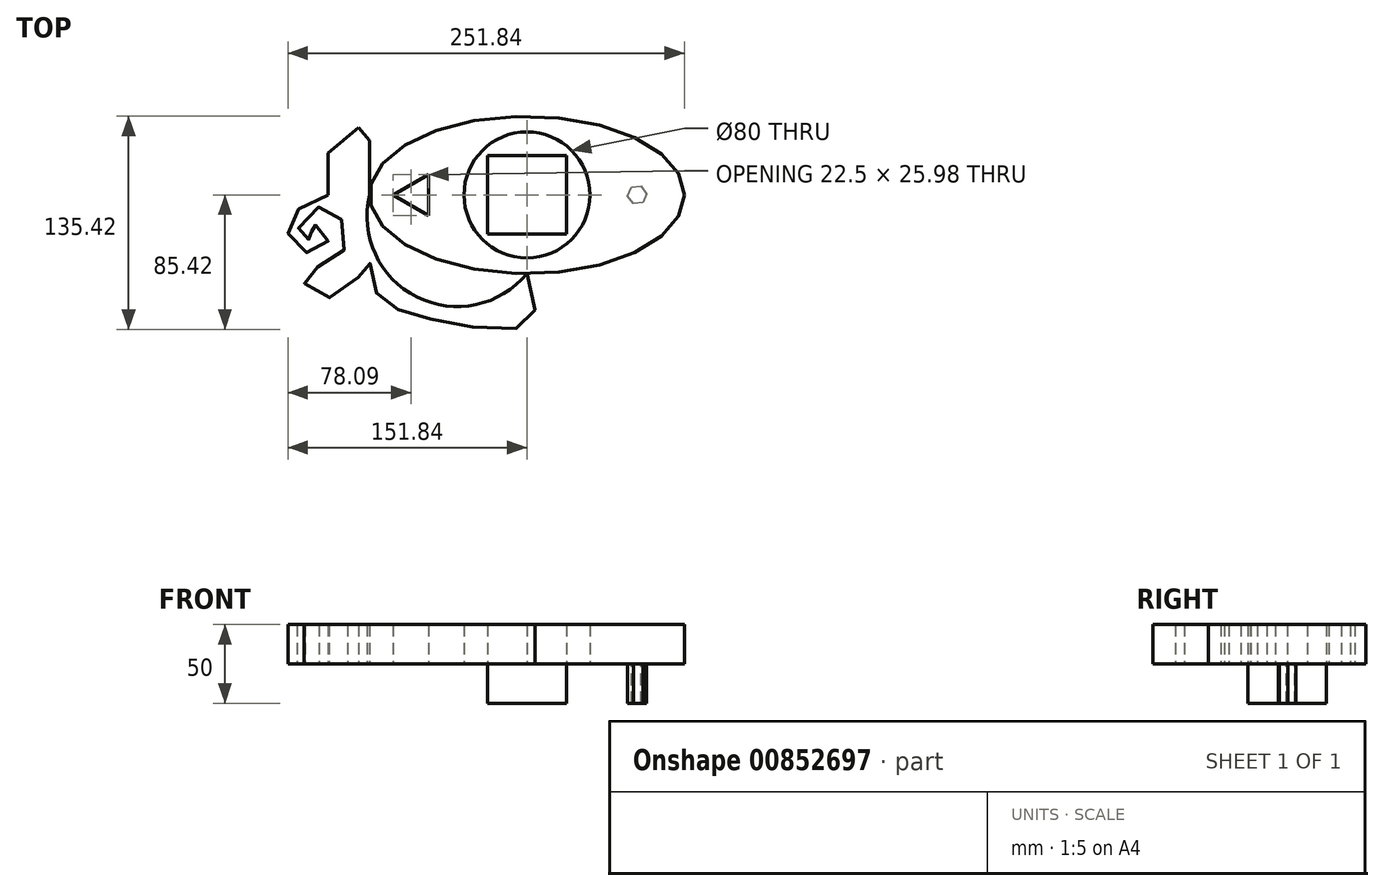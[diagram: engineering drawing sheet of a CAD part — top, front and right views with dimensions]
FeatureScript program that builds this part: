
annotation { "Feature Type Name" : "Feature", "Feature Type Description" : "" }
export const myFeature = defineFeature(function(context is Context, id is Id, definition is map)
    precondition{}
    {
        {
            var Q0;
            Q0=qCreatedBy(makeId("Top.planeOp"),FACE);
            var sketch = newSketch(context, id + "F0", { "sketchPlane" : qUnion([Q0])});
            skLineSegment(sketch, "E0.bottom", {"start": v(25, 25) * mm, "end": v(-25, 25) * mm});
            skLineSegment(sketch, "E0.top", {"start": v(25, -25) * mm, "end": v(-25, -25) * mm});
            skLineSegment(sketch, "E0.left", {"start": v(25, 25) * mm, "end": v(25, -25) * mm});
            skLineSegment(sketch, "E0.right", {"start": v(-25, 25) * mm, "end": v(-25, -25) * mm});
            skPoint(sketch, "E0.middle", {"position": v(0, 0) * mm});
            skCircle(sketch, "E1", {"center": v(0, 0) * mm, "radius": 40 * mm});
            skEllipse(sketch, "E2", {"center": v(0, 0) * mm, "majorRadius": 100 * mm, "minorRadius": 50 * mm, "majorAxis": v(1, 0)});
            skPoint(sketch, "E3", {"position": v(-100, 0) * mm});
            skPoint(sketch, "E4", {"position": v(0, -50) * mm});
            skArc(sketch, "E5", {"start": v(-100, 0) * mm, "mid": v(-69.93, -64.85) * mm, "end": v(0, -50) * mm});
            skPoint(sketch, "E6", {"position": v(-70, 0) * mm});
            skPoint(sketch, "E7", {"position": v(70, 0) * mm});
            skCircle(sketch, "E8.cCircle", {"center": v(70, 0) * mm, "radius": 5.25 * mm, "construction": true});
            skLineSegment(sketch, "E8.0", {"start": v(72.5, 5.53) * mm, "end": v(76.03, 0.6) * mm});
            skLineSegment(sketch, "E8.1", {"start": v(76.03, 0.6) * mm, "end": v(73.54, -4.92) * mm});
            skLineSegment(sketch, "E8.2", {"start": v(73.54, -4.92) * mm, "end": v(67.5, -5.53) * mm});
            skLineSegment(sketch, "E8.3", {"start": v(67.5, -5.53) * mm, "end": v(63.97, -0.6) * mm});
            skLineSegment(sketch, "E8.4", {"start": v(63.97, -0.6) * mm, "end": v(66.46, 4.92) * mm});
            skLineSegment(sketch, "E8.5", {"start": v(66.46, 4.92) * mm, "end": v(72.5, 5.53) * mm});
            skPoint(sketch, "E8.0.midPoint", {"position": v(74.26, 3.06) * mm});
            skCircle(sketch, "E9.cCircle", {"center": v(-70, 0) * mm, "radius": 15 * mm, "construction": true});
            skLineSegment(sketch, "E9.0", {"start": v(-85, 0) * mm, "end": v(-62.5, 13) * mm});
            skLineSegment(sketch, "E9.1", {"start": v(-62.5, 13) * mm, "end": v(-62.5, -13) * mm});
            skLineSegment(sketch, "E9.2", {"start": v(-62.5, -13) * mm, "end": v(-85, 0) * mm});
            skLineSegment(sketch, "E10", {"start": v(-100, 0) * mm, "end": v(-126.42, 0) * mm});
            skLineSegment(sketch, "E11", {"start": v(-126.42, 0) * mm, "end": v(-126.42, 26.64) * mm});
            skLineSegment(sketch, "E12", {"start": v(-126.42, 26.64) * mm, "end": v(-107.04, 42.87) * mm});
            skLineSegment(sketch, "E13", {"start": v(-107.04, 42.87) * mm, "end": v(-100, 34.47) * mm});
            skLineSegment(sketch, "E14", {"start": v(-100, 34.47) * mm, "end": v(-100, 0) * mm});
            skFitSpline(sketch, "E15", {"points": [v(-126.42, 0) * mm, v(-149.68, -14.06) * mm, v(-147.74, -32.48) * mm, v(-128.84, -34.41) * mm, v(-129.33, -19.4) * mm, v(-140.95, -22.78) * mm, v(-132.23, -23.75) * mm, v(-144.35, -29.08) * mm, v(-140.95, -14.06) * mm, v(-124.48, -8.73) * mm, v(-114.79, -32.48) * mm, v(-136.1, -47.5) * mm, v(-140.95, -56.94) * mm, v(-117.45, -63.73) * mm, v(-100.74, -42.17) * mm, v(-96.38, -60.58) * mm, v(-79.9, -73.42) * mm, v(-40.17, -83.1) * mm, v(2.47, -80.44) * mm, v(0, -50) * mm], "startDerivative": vector(-480.16, -179.48) * mm, "endDerivative": vector(-187.13, 577.46) * mm});
            skSolve(sketch);
        }
        {
            var Q0;
            Q0=makeQuery(id+"F0.imprint","IMPRINT",FACE,{"disambiguationData":[TD([[makeQuery(id+"F0.imprint","IMPRINT",EDGE,{"derivedFrom":sQuery(id+"F0.wireOp",EDGE,"E1")}),-1.0]])]});
            var Q1;
            Q1=makeQuery(id+"F0.imprint","IMPRINT",FACE,{"disambiguationData":[TD([[makeQuery(id+"F0.imprint","IMPRINT",EDGE,{"derivedFrom":sQuery(id+"F0.wireOp",EDGE,"E0.bottom")}),1.0]])]});
            var Q2;
            Q2=makeQuery(id+"F0.imprint","IMPRINT",FACE,{"disambiguationData":[TD([[makeQuery(id+"F0.imprint","IMPRINT",EDGE,{"derivedFrom":sQuery(id+"F0.wireOp",EDGE,"E5")}),-1.0]])]});
            var Q3;
            Q3=makeQuery(id+"F0.imprint","IMPRINT",FACE,{"disambiguationData":[TD([[makeQuery(id+"F0.imprint","IMPRINT",EDGE,{"derivedFrom":sQuery(id+"F0.wireOp",EDGE,"E10")}),-1.0]])]});
            var Q4;
            Q4=makeQuery(id+"F0.imprint","IMPRINT",FACE,{"disambiguationData":[TD([[makeQuery(id+"F0.imprint","IMPRINT",EDGE,{"derivedFrom":sQuery(id+"F0.wireOp",EDGE,"E8.0")}),-1.0]])]});
            extrude(context, id + "F1", {"entities" : qUnion([Q0, Q1, Q2, Q3, Q4]), "depth" : 25 * mm, "offsetDistance" : 25 * mm});
        }
        {
            var Q0;
            Q0=makeQuery(id+"F0.imprint","IMPRINT",FACE,{"disambiguationData":[TD([[makeQuery(id+"F0.imprint","IMPRINT",EDGE,{"derivedFrom":sQuery(id+"F0.wireOp",EDGE,"E8.0")}),-1.0]])]});
            var Q1;
            Q1=makeQuery(id+"F0.imprint","IMPRINT",FACE,{"disambiguationData":[TD([[makeQuery(id+"F0.imprint","IMPRINT",EDGE,{"derivedFrom":sQuery(id+"F0.wireOp",EDGE,"E0.bottom")}),1.0]])]});
            extrude(context, id + "F2", {"entities" : qUnion([Q0, Q1]), "operationType" : NewBodyOperationType.ADD, "oppositeDirection" : true, "depth" : 25 * mm, "offsetDistance" : 25 * mm});
        }
    });
